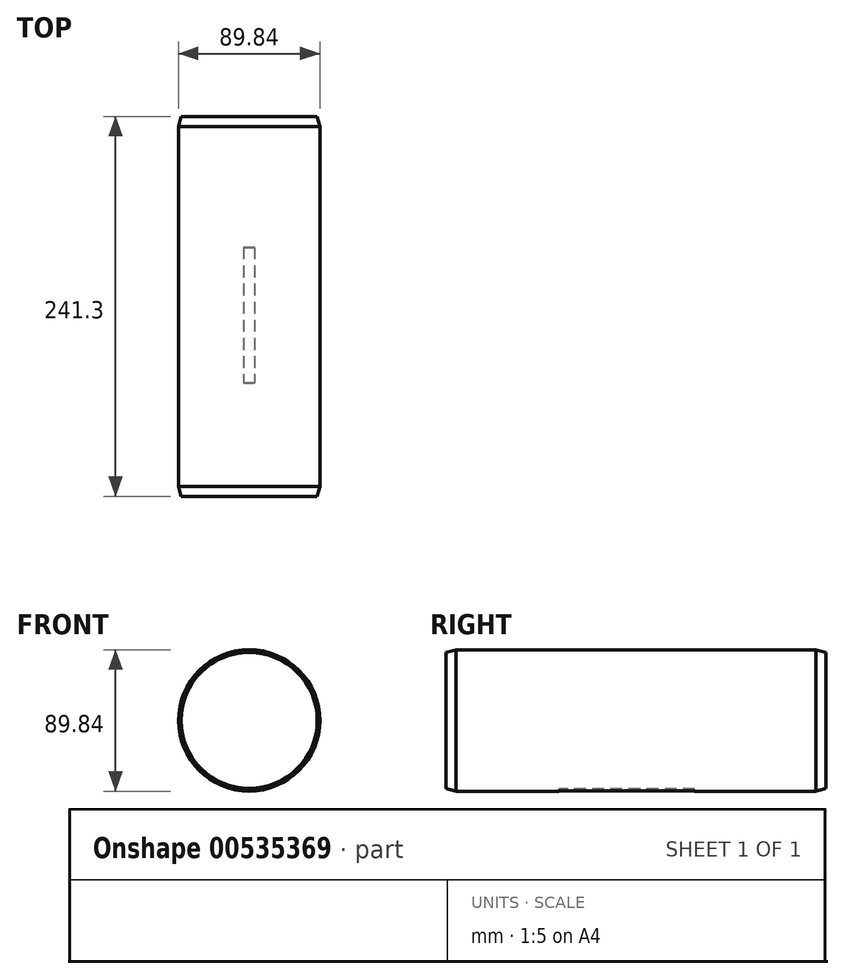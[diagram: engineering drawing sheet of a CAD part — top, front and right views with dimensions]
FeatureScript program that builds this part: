
annotation { "Feature Type Name" : "Feature", "Feature Type Description" : "" }
export const myFeature = defineFeature(function(context is Context, id is Id, definition is map)
    precondition{}
    {
        {
            var Q0;
            Q0=qCreatedBy(makeId("Front.planeOp"),FACE);
            var sketch = newSketch(context, id + "F0", { "sketchPlane" : qUnion([Q0])});
            skCircle(sketch, "E0", {"center": v(0, 0) * mm, "radius": 44.92 * mm});
            skSolve(sketch);
        }
        {
            var Q0;
            Q0=qSketchRegion(id+"F0",true);
            extrude(context, id + "F1", {"entities" : qUnion([Q0]), "depth" : 241.3 * mm, "offsetDistance" : 25.4 * mm});
        }
        {
            var Q0;
            Q0=makeQuery(id+"F1.opExtrude","CAP_EDGE",EDGE,{"disambiguationData":[OSD([sQuery(id+"F0.wireOp",EDGE,"E0")])],"isStart":false});
            var Q1;
            Q1=makeQuery(id+"F1.opExtrude","CAP_EDGE",EDGE,{"disambiguationData":[OSD([sQuery(id+"F0.wireOp",EDGE,"E0")])],"isStart":true});
            chamfer(context, id + "F2", {"entities" : qUnion([Q0, Q1]), "chamferType" : ChamferType.OFFSET_ANGLE, "width" : 6.35 * mm, "oppositeDirection" : true, "angle" : 15 * degree, "tangentPropagation" : true});
        }
        {
            var Q0;
            Q0=makeQuery(id+"F1.opExtrude","CAP_FACE",FACE,{"disambiguationData":[OSD([sQuery(id+"F0.wireOp",EDGE,"E0")])],"isStart":false});
            cPlane(context, id + "F3", {"entities" : qUnion([Q0]), "cplaneType" : CPlaneType.OFFSET, "offset" : 72 * mm, "oppositeDirection" : true, "width" : 152.4 * mm, "height" : 152.4 * mm});
        }
        {
            var Q0;
            Q0=qCreatedBy(id+"F3.planeOp",FACE);
            var sketch = newSketch(context, id + "F4", { "sketchPlane" : qUnion([Q0])});
            skCircle(sketch, "E1", {"center": v(0, -48.1) * mm, "radius": 4.76 * mm});
            skSolve(sketch);
        }
        {
            var Q0;
            Q0 = qSketchRegion(id + "F4", true);
            extrude(context, id + "F5", {"entities" : qUnion([Q0]), "operationType" : NewBodyOperationType.REMOVE, "oppositeDirection" : true, "depth" : 86 * mm, "offsetDistance" : 25.4 * mm});
        }
    });
